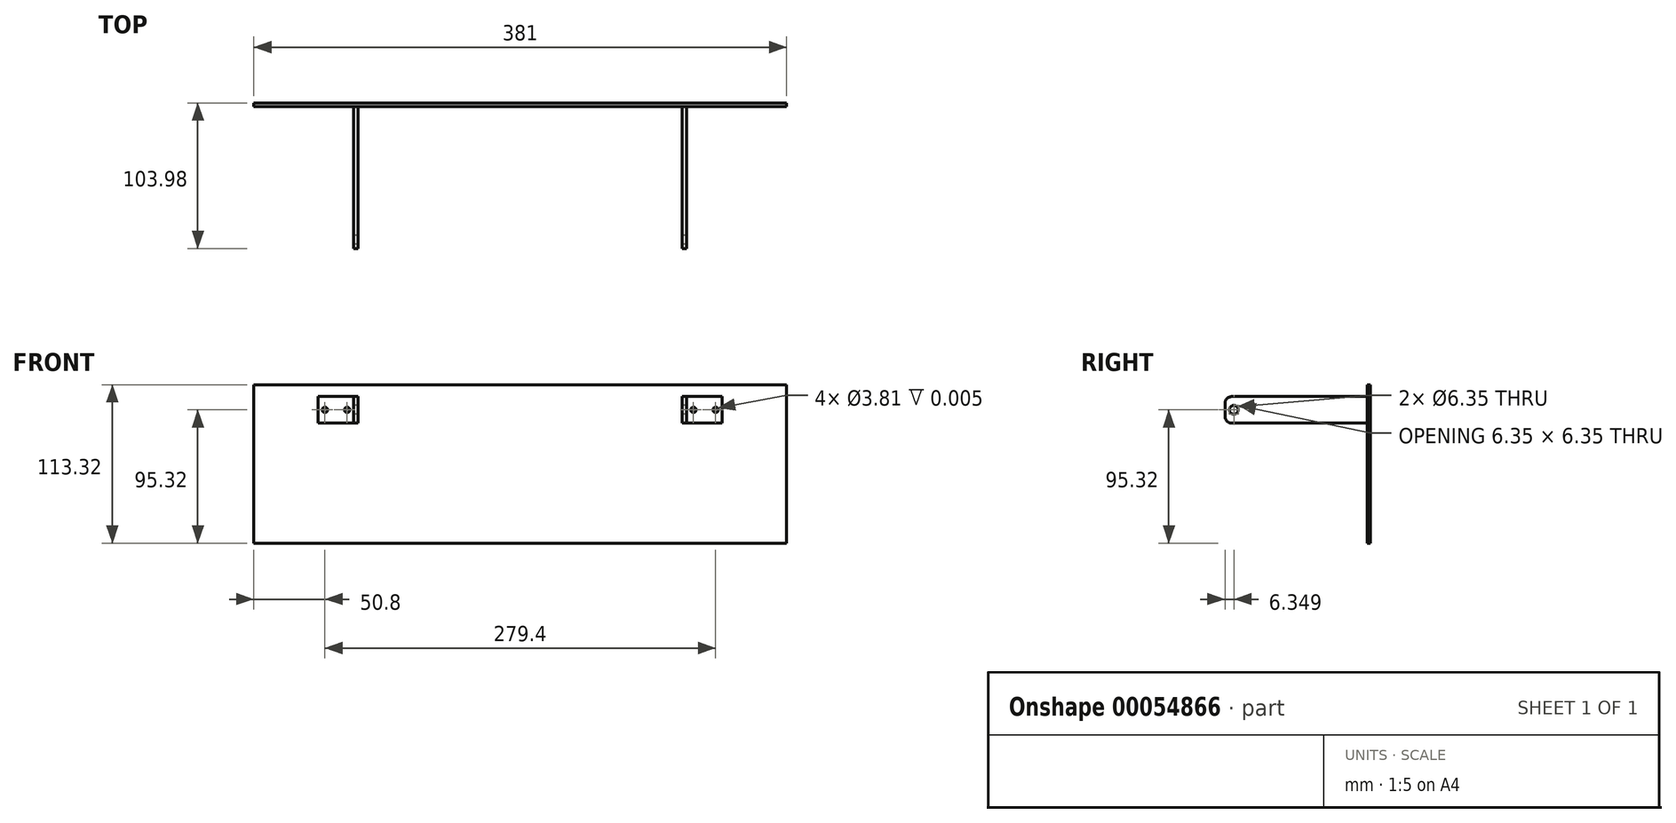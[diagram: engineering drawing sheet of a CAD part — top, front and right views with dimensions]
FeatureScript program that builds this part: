
annotation { "Feature Type Name" : "Feature", "Feature Type Description" : "" }
export const myFeature = defineFeature(function(context is Context, id is Id, definition is map)
    precondition{}
    {
        {
            var Q0;
            Q0=qCreatedBy(makeId("Front.planeOp"),FACE);
            var sketch = newSketch(context, id + "F0", { "sketchPlane" : qUnion([Q0])});
            skLineSegment(sketch, "E0.rect.bottom", {"start": v(190.5, 36) * mm, "end": v(-190.5, 36) * mm});
            skLineSegment(sketch, "E0.rect.left", {"start": v(190.5, 36) * mm, "end": v(190.5, -36) * mm});
            skLineSegment(sketch, "E0.rect.right", {"start": v(-190.5, 36) * mm, "end": v(-190.5, -36) * mm});
            skPoint(sketch, "E0.rect.middle", {"position": v(0, 0) * mm});
            skLineSegment(sketch, "E1.top", {"start": v(-190.5, -77.32) * mm, "end": v(190.5, -77.32) * mm});
            skLineSegment(sketch, "E1.left", {"start": v(-190.5, -36) * mm, "end": v(-190.5, -77.32) * mm});
            skLineSegment(sketch, "E1.right", {"start": v(190.5, -36) * mm, "end": v(190.5, -77.32) * mm});
            skSolve(sketch);
        }
        {
            var Q0;
            Q0=makeQuery(id+"F0.imprint","IMPRINT",FACE,{"disambiguationData":[TD([[makeQuery(id+"F0.imprint","IMPRINT",EDGE,{"derivedFrom":sQuery(id+"F0.wireOp",EDGE,"E0.rect.bottom")}),1.0]])]});
            extrude(context, id + "F1", {"entities" : qUnion([Q0]), "depth" : 2.38 * mm});
        }
        {
            var Q0;
            Q0=makeQuery(id+"F1.opExtrude","CAP_FACE",FACE,{"disambiguationData":[OSD([sQuery(id+"F0.wireOp",EDGE,"E0.rect.bottom"),sQuery(id+"F0.wireOp",EDGE,"E0.rect.left"),sQuery(id+"F0.wireOp",EDGE,"E0.rect.right"),sQuery(id+"F0.wireOp",EDGE,"E1.top"),sQuery(id+"F0.wireOp",EDGE,"E1.left"),sQuery(id+"F0.wireOp",EDGE,"E1.right")])],"isStart":false});
            var sketch = newSketch(context, id + "F2", { "sketchPlane" : qUnion([Q0])});
            skPoint(sketch, "E2", {"position": v(0, 18) * mm});
            skLineSegment(sketch, "E3", {"start": v(0, 18) * mm, "end": v(115.89, 18) * mm});
            skLineSegment(sketch, "E4", {"start": v(0, 18) * mm, "end": v(-115.89, 18) * mm});
            skLineSegment(sketch, "E5", {"start": v(119.06, 18) * mm, "end": v(119.06, -77.25) * mm});
            skLineSegment(sketch, "E6", {"start": v(-119.06, -77.25) * mm, "end": v(-119.06, 18) * mm});
            skPoint(sketch, "E7", {"position": v(115.89, -77.25) * mm});
            skPoint(sketch, "E8", {"position": v(-115.89, -77.25) * mm});
            skLineSegment(sketch, "E9", {"start": v(115.89, 18) * mm, "end": v(115.89, 27.53) * mm});
            skLineSegment(sketch, "E10", {"start": v(115.89, 18) * mm, "end": v(115.89, 8.48) * mm});
            skLineSegment(sketch, "E11.bottom", {"start": v(115.89, 27.53) * mm, "end": v(119.06, 27.53) * mm});
            skLineSegment(sketch, "E11.top", {"start": v(115.89, 8.48) * mm, "end": v(119.06, 8.48) * mm});
            skLineSegment(sketch, "E11.left", {"start": v(115.89, 27.53) * mm, "end": v(115.89, 8.48) * mm});
            skLineSegment(sketch, "E11.right", {"start": v(119.06, 27.53) * mm, "end": v(119.06, 8.48) * mm});
            skLineSegment(sketch, "E12.right", {"start": v(-115.89, 27.53) * mm, "end": v(-115.89, 8.47) * mm});
            skLineSegment(sketch, "E13", {"start": v(-119.06, 18) * mm, "end": v(-119.06, 27.53) * mm});
            skLineSegment(sketch, "E12.bottom", {"start": v(-119.06, 27.53) * mm, "end": v(-115.89, 27.53) * mm});
            skLineSegment(sketch, "E14", {"start": v(-119.06, 18) * mm, "end": v(-119.06, 8.47) * mm});
            skLineSegment(sketch, "E12.top", {"start": v(-119.06, 8.47) * mm, "end": v(-115.89, 8.47) * mm});
            skPoint(sketch, "E15", {"position": v(-115.89, 18) * mm});
            skSolve(sketch);
        }
        {
            var Q0;
            Q0 = qSketchRegion(id + "F2", true);
            extrude(context, id + "F3", {"entities" : qUnion([Q0]), "depth" : 101.6 * mm});
        }
        {
            var Q0;
            Q0=makeQuery(id+"F3.opExtrude","SWEPT_FACE",FACE,{"disambiguationData":[OSD([sQuery(id+"F2.wireOp",EDGE,"E13"),sQuery(id+"F2.wireOp",EDGE,"E14")])]});
            var sketch = newSketch(context, id + "F4", { "sketchPlane" : qUnion([Q0])});
            skLineSegment(sketch, "E16", {"start": v(2.38, 18) * mm, "end": v(97.63, 18) * mm});
            skCircle(sketch, "E17", {"center": v(97.63, 18) * mm, "radius": 3.18 * mm});
            skSolve(sketch);
        }
        {
            var Q0;
            Q0 = qSketchRegion(id + "F4", true);
            extrude(context, id + "F5", {"entities" : qUnion([Q0]), "operationType" : NewBodyOperationType.REMOVE, "oppositeDirection" : true, "depth" : 25000 * mm});
        }
        {
            var Q0;
            Q0=makeQuery(id+"F3.opExtrude","CAP_EDGE",EDGE,{"disambiguationData":[OSD([sQuery(id+"F2.wireOp",EDGE,"E12.bottom")])],"isStart":false});
            fillet(context, id + "F6", {"entities" : qUnion([Q0]), "radius" : 5 * mm, "tangentPropagation" : true, "allowEdgeOverflow" : false});
        }
        {
            var Q0;
            Q0=makeQuery(id+"F3.opExtrude","CAP_EDGE",EDGE,{"disambiguationData":[OSD([sQuery(id+"F2.wireOp",EDGE,"E12.top")])],"isStart":false});
            fillet(context, id + "F7", {"entities" : qUnion([Q0]), "radius" : 5 * mm, "tangentPropagation" : true, "allowEdgeOverflow" : false});
        }
        {
            var Q0;
            Q0=makeQuery(id+"F3.opExtrude","CAP_EDGE",EDGE,{"disambiguationData":[OSD([sQuery(id+"F2.wireOp",EDGE,"E11.bottom")])],"isStart":false});
            var Q1;
            Q1=makeQuery(id+"F3.opExtrude","CAP_EDGE",EDGE,{"disambiguationData":[OSD([sQuery(id+"F2.wireOp",EDGE,"E11.top")])],"isStart":false});
            fillet(context, id + "F8", {"entities" : qUnion([Q0, Q1]), "radius" : 5 * mm, "tangentPropagation" : true, "allowEdgeOverflow" : false});
        }
        {
            var Q0;
            {var subQ7=sQuery(id+"F2.wireOp",EDGE,"E11.bottom");Q0=makeQuery(id+"F2.imprint","IMPRINT",FACE,{"disambiguationData":[TD([[makeQuery(id+"F2.imprint","IMPRINT",EDGE,{"derivedFrom":subQ7}),1.0]])]});}
            var sketch = newSketch(context, id + "F9", { "sketchPlane" : qUnion([Q0])});
            skLineSegment(sketch, "E18", {"start": v(0, 0) * mm, "end": v(-115.89, 0) * mm});
            skLineSegment(sketch, "E19", {"start": v(-115.89, 0) * mm, "end": v(-119.06, 0) * mm});
            skLineSegment(sketch, "E20", {"start": v(-119.06, 0) * mm, "end": v(-119.06, 18) * mm});
            skLineSegment(sketch, "E21", {"start": v(-119.06, 18) * mm, "end": v(-119.06, 27.52) * mm});
            skLineSegment(sketch, "E22", {"start": v(-119.06, 18) * mm, "end": v(-119.06, 8.47) * mm});
            skLineSegment(sketch, "E23.bottom", {"start": v(-119.06, 27.52) * mm, "end": v(-144.46, 27.52) * mm});
            skLineSegment(sketch, "E23.top", {"start": v(-119.06, 8.47) * mm, "end": v(-144.46, 8.47) * mm});
            skLineSegment(sketch, "E23.left", {"start": v(-119.06, 27.52) * mm, "end": v(-119.06, 8.47) * mm});
            skLineSegment(sketch, "E23.right", {"start": v(-144.46, 27.52) * mm, "end": v(-144.46, 8.47) * mm});
            skLineSegment(sketch, "E24", {"start": v(0, 0) * mm, "end": v(0, 35.3) * mm});
            skLineSegment(sketch, "E25.MirrorCS", {"start": v(119.06, 18) * mm, "end": v(119.06, 8.47) * mm});
            skLineSegment(sketch, "E26.MirrorCS", {"start": v(119.06, 18) * mm, "end": v(119.06, 27.52) * mm});
            skLineSegment(sketch, "E27.MirrorCS", {"start": v(119.06, 27.52) * mm, "end": v(119.06, 8.47) * mm});
            skLineSegment(sketch, "E28.MirrorCS", {"start": v(115.89, 0) * mm, "end": v(119.06, 0) * mm});
            skLineSegment(sketch, "E29.MirrorCS", {"start": v(119.06, 0) * mm, "end": v(119.06, 18) * mm});
            skLineSegment(sketch, "E30.MirrorCS", {"start": v(144.46, 27.52) * mm, "end": v(144.46, 8.47) * mm});
            skLineSegment(sketch, "E31.MirrorCS", {"start": v(119.06, 8.47) * mm, "end": v(144.46, 8.47) * mm});
            skLineSegment(sketch, "E32.MirrorCS", {"start": v(119.06, 27.52) * mm, "end": v(144.46, 27.52) * mm});
            skLineSegment(sketch, "E33.MirrorCS", {"start": v(0, 0) * mm, "end": v(115.89, 0) * mm});
            skPoint(sketch, "E34", {"position": v(-131.76, 18) * mm});
            skPoint(sketch, "E34.positionSnap0", {"position": v(-144.46, 18) * mm});
            skPoint(sketch, "E34.positionSnap1", {"position": v(-131.76, 27.52) * mm});
            skLineSegment(sketch, "E35", {"start": v(-139.7, 18) * mm, "end": v(-123.83, 18) * mm});
            skCircle(sketch, "E36", {"center": v(-139.7, 18) * mm, "radius": 1.9 * mm});
            skLineSegment(sketch, "E37", {"start": v(-131.76, 27.52) * mm, "end": v(-131.76, 8.47) * mm});
            skCircle(sketch, "E38.MirrorC", {"center": v(-123.83, 18) * mm, "radius": 1.9 * mm});
            skPoint(sketch, "E39.MirrorP", {"position": v(131.76, 18) * mm});
            skLineSegment(sketch, "E40.MirrorCS", {"start": v(131.76, 27.52) * mm, "end": v(131.76, 8.47) * mm});
            skLineSegment(sketch, "E41.MirrorCS", {"start": v(139.7, 18) * mm, "end": v(123.83, 18) * mm});
            skCircle(sketch, "E42.MirrorC", {"center": v(139.7, 18) * mm, "radius": 1.9 * mm});
            skPoint(sketch, "E43.MirrorP", {"position": v(131.76, 27.52) * mm});
            skPoint(sketch, "E44.MirrorP", {"position": v(144.46, 18) * mm});
            skCircle(sketch, "E45.MirrorC", {"center": v(123.83, 18) * mm, "radius": 1.9 * mm});
            skSolve(sketch);
        }
        {
            var Q0;
            Q0 = qSketchRegion(id + "F9", true);
            extrude(context, id + "F10", {"entities" : qUnion([Q0]), "operationType" : NewBodyOperationType.ADD, "depth" : 1 / 203.2 * mm});
        }
    });
